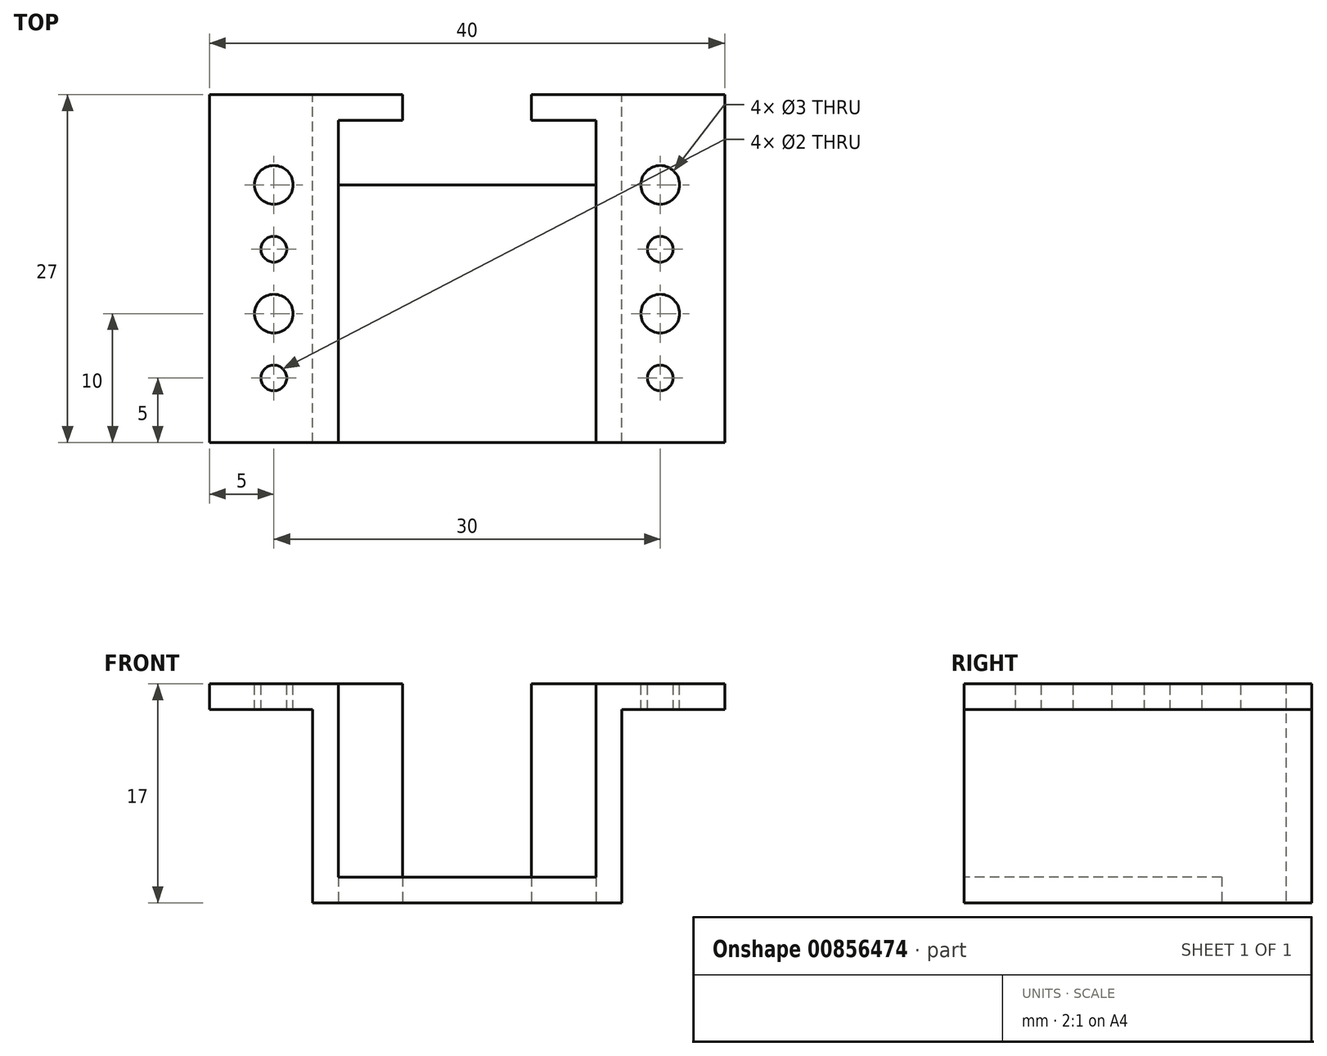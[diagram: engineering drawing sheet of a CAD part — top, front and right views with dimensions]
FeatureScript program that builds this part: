
annotation { "Feature Type Name" : "Feature", "Feature Type Description" : "" }
export const myFeature = defineFeature(function(context is Context, id is Id, definition is map)
    precondition{}
    {
        {
            var Q0;
            Q0=qCreatedBy(makeId("Front.planeOp"),FACE);
            var sketch = newSketch(context, id + "F0", { "sketchPlane" : qUnion([Q0])});
            skLineSegment(sketch, "E0.bottom", {"start": v(12, 0) * mm, "end": v(-12, 0) * mm});
            skLineSegment(sketch, "E0.top", {"start": v(12, -17) * mm, "end": v(-12, -17) * mm});
            skLineSegment(sketch, "E0.left", {"start": v(12, 0) * mm, "end": v(12, -17) * mm});
            skLineSegment(sketch, "E0.right", {"start": v(-12, 0) * mm, "end": v(-12, -17) * mm});
            skLineSegment(sketch, "E1.bottom", {"start": v(20, 0) * mm, "end": v(-20, 0) * mm});
            skLineSegment(sketch, "E1.top", {"start": v(20, -2) * mm, "end": v(-20, -2) * mm});
            skLineSegment(sketch, "E1.left", {"start": v(20, 0) * mm, "end": v(20, -2) * mm});
            skLineSegment(sketch, "E1.right", {"start": v(-20, 0) * mm, "end": v(-20, -2) * mm});
            skSolve(sketch);
        }
        {
            var Q0;
            Q0 = qSketchRegion(id + "F0", true);
            extrude(context, id + "F1", {"entities" : qUnion([Q0]), "depth" : 27 * mm, "offsetDistance" : 25 * mm});
        }
        {
            var Q0;
            Q0=makeQuery(id+"F1.opExtrude","SWEPT_FACE",FACE,{"disambiguationData":[OSD([sQuery(id+"F0.wireOp",EDGE,"E0.top")])]});
            var sketch = newSketch(context, id + "F2", { "sketchPlane" : qUnion([Q0])});
            skLineSegment(sketch, "E2.bottom", {"start": v(10, 2) * mm, "end": v(-10, 2) * mm});
            skLineSegment(sketch, "E2.top", {"start": v(10, 7) * mm, "end": v(-10, 7) * mm});
            skLineSegment(sketch, "E2.left", {"start": v(10, 2) * mm, "end": v(10, 7) * mm});
            skLineSegment(sketch, "E2.right", {"start": v(-10, 2) * mm, "end": v(-10, 7) * mm});
            skPoint(sketch, "E3.centerSnap0", {"position": v(0, 27) * mm});
            skLineSegment(sketch, "E4", {"start": v(0, 7) * mm, "end": v(0, 27) * mm, "construction": true});
            skSolve(sketch);
        }
        {
            var Q0;
            Q0 = qSketchRegion(id + "F2", true);
            extrude(context, id + "F3", {"entities" : qUnion([Q0]), "operationType" : NewBodyOperationType.REMOVE, "endBound" : BoundingType.THROUGH_ALL, "oppositeDirection" : true, "depth" : 25 * mm, "offsetDistance" : 25 * mm});
        }
        {
            var Q0;
            Q0=makeQuery(id+"F1.opExtrude","CAP_FACE",FACE,{"disambiguationData":[OSD([sQuery(id+"F0.wireOp",EDGE,"E0.top"),sQuery(id+"F0.wireOp",EDGE,"E0.left"),sQuery(id+"F0.wireOp",EDGE,"E0.right"),sQuery(id+"F0.wireOp",EDGE,"E1.bottom"),sQuery(id+"F0.wireOp",EDGE,"E1.top"),sQuery(id+"F0.wireOp",EDGE,"E1.left"),sQuery(id+"F0.wireOp",EDGE,"E1.right")])],"isStart":true});
            var sketch = newSketch(context, id + "F4", { "sketchPlane" : qUnion([Q0])});
            skLineSegment(sketch, "E5.bottom", {"start": v(-5, 0) * mm, "end": v(5, 0) * mm});
            skLineSegment(sketch, "E5.top", {"start": v(-5, -17) * mm, "end": v(5, -17) * mm});
            skLineSegment(sketch, "E5.left", {"start": v(-5, 0) * mm, "end": v(-5, -17) * mm});
            skLineSegment(sketch, "E5.right", {"start": v(5, 0) * mm, "end": v(5, -17) * mm});
            skSolve(sketch);
        }
        {
            var Q0;
            Q0 = qSketchRegion(id + "F4", true);
            extrude(context, id + "F5", {"entities" : qUnion([Q0]), "operationType" : NewBodyOperationType.REMOVE, "endBound" : BoundingType.UP_TO_NEXT, "oppositeDirection" : true, "depth" : 25 * mm, "offsetDistance" : 25 * mm});
        }
        {
            var Q0;
            Q0=makeQuery(id+"F1.opExtrude","CAP_FACE",FACE,{"disambiguationData":[OSD([sQuery(id+"F0.wireOp",EDGE,"E0.top"),sQuery(id+"F0.wireOp",EDGE,"E0.left"),sQuery(id+"F0.wireOp",EDGE,"E0.right"),sQuery(id+"F0.wireOp",EDGE,"E1.bottom"),sQuery(id+"F0.wireOp",EDGE,"E1.top"),sQuery(id+"F0.wireOp",EDGE,"E1.left"),sQuery(id+"F0.wireOp",EDGE,"E1.right")])],"isStart":false});
            var sketch = newSketch(context, id + "F6", { "sketchPlane" : qUnion([Q0])});
            skLineSegment(sketch, "E6.bottom", {"start": v(10, -15) * mm, "end": v(-10, -15) * mm});
            skLineSegment(sketch, "E6.top", {"start": v(10, -2) * mm, "end": v(-10, -2) * mm});
            skLineSegment(sketch, "E6.left", {"start": v(10, -15) * mm, "end": v(10, -2) * mm});
            skLineSegment(sketch, "E6.right", {"start": v(-10, -15) * mm, "end": v(-10, -2) * mm});
            skSolve(sketch);
        }
        {
            var Q0;
            Q0 = qSketchRegion(id + "F6", true);
            var Q1;
            Q1=makeQuery(id+"F5.boolean.opBoolean","SPLIT",FACE,{"disambiguationData":[TD([makeQuery(id+"F3.boolean.opBoolean","COPY",FACE,{"derivedFrom":makeQuery(id+"F3.opExtrude","SWEPT_FACE",FACE,{"disambiguationData":[OSD([sQuery(id+"F2.wireOp",EDGE,"E2.right")])]})})])],"derivedFrom":makeQuery(id+"F3.boolean.opBoolean","COPY",FACE,{"derivedFrom":makeQuery(id+"F3.opExtrude","SWEPT_FACE",FACE,{"disambiguationData":[OSD([sQuery(id+"F2.wireOp",EDGE,"E2.bottom")])]})})});
            extrude(context, id + "F7", {"entities" : qUnion([Q0]), "operationType" : NewBodyOperationType.REMOVE, "endBound" : BoundingType.UP_TO_SURFACE, "oppositeDirection" : true, "depth" : 25 * mm, "endBoundEntityFace" : qUnion([Q1]), "offsetDistance" : 25 * mm});
        }
        {
            var Q0;
            Q0=makeQuery(id+"F1.opExtrude","SWEPT_FACE",FACE,{"disambiguationData":[OSD([sQuery(id+"F0.wireOp",EDGE,"E1.bottom")])]});
            var sketch = newSketch(context, id + "F8", { "sketchPlane" : qUnion([Q0])});
            skLineSegment(sketch, "E7.bottom", {"start": v(-10, -2) * mm, "end": v(10, -2) * mm});
            skLineSegment(sketch, "E7.top", {"start": v(-10, -27) * mm, "end": v(10, -27) * mm});
            skLineSegment(sketch, "E7.left", {"start": v(-10, -2) * mm, "end": v(-10, -27) * mm});
            skLineSegment(sketch, "E7.right", {"start": v(10, -2) * mm, "end": v(10, -27) * mm});
            skSolve(sketch);
        }
        {
            var Q0;
            {var subQ0=sQuery(id+"F8.wireOp",EDGE,"E7.top");Q0=makeQuery(id+"F8.imprint","IMPRINT",FACE,{"disambiguationData":[TD([[makeQuery(id+"F8.imprint","IMPRINT",EDGE,{"derivedFrom":subQ0}),-1.0]])]});}
            var Q1;
            {var subQ1=makeQuery(id+"F1.opExtrude","SWEPT_FACE",FACE,{"disambiguationData":[OSD([sQuery(id+"F0.wireOp",EDGE,"E1.bottom")])]});var subQ2=makeQuery(id+"F3.boolean.opBoolean","INTERSECT",EDGE,{"derivedFrom":[subQ1,makeQuery(id+"F3.opExtrude","SWEPT_FACE",FACE,{"disambiguationData":[OSD([sQuery(id+"F2.wireOp",EDGE,"E2.top")])]})]});Q1=makeQuery(id+"F8.imprint","IMPRINT",FACE,{"disambiguationData":[TD([[makeQuery(id+"F8.imprint","IMPRINT",EDGE,{"derivedFrom":subQ2}),1.0]])]});}
            extrude(context, id + "F9", {"entities" : qUnion([Q0, Q1]), "operationType" : NewBodyOperationType.REMOVE, "endBound" : BoundingType.UP_TO_NEXT, "oppositeDirection" : true, "depth" : 25 * mm, "offsetDistance" : 25 * mm});
        }
        {
            var Q0;
            {var subQ0=sQuery(id+"F0.wireOp",EDGE,"E1.left");var subQ3=sQuery(id+"F0.wireOp",EDGE,"E1.bottom");var subQ8=makeQuery(id+"F1.opExtrude","SWEPT_FACE",FACE,{"disambiguationData":[OSD([subQ3])]});Q0=makeQuery(id+"F9.boolean.opBoolean","SPLIT",FACE,{"disambiguationData":[TD([makeQuery(id+"F1.opExtrude","SWEPT_FACE",FACE,{"disambiguationData":[OSD([subQ0])]})])],"derivedFrom":subQ8});}
            var sketch = newSketch(context, id + "F10", { "sketchPlane" : qUnion([Q0])});
            skCircle(sketch, "E8", {"center": v(15, -22) * mm, "radius": 1 * mm});
            skPoint(sketch, "E8.centerSnap0", {"position": v(15, -27) * mm});
            skCircle(sketch, "E9", {"center": v(15, -17) * mm, "radius": 1.5 * mm});
            skCircle(sketch, "E10", {"center": v(15, -12) * mm, "radius": 1 * mm});
            skCircle(sketch, "E11", {"center": v(15, -7) * mm, "radius": 1.5 * mm});
            skSolve(sketch);
        }
        {
            var Q0;
            Q0 = qSketchRegion(id + "F10", true);
            extrude(context, id + "F11", {"entities" : qUnion([Q0]), "operationType" : NewBodyOperationType.REMOVE, "endBound" : BoundingType.THROUGH_ALL, "oppositeDirection" : true, "depth" : 25 * mm, "offsetDistance" : 25 * mm});
        }
        {
            var Q0;
            {var subQ0=sQuery(id+"F0.wireOp",EDGE,"E1.right");var subQ2=sQuery(id+"F0.wireOp",EDGE,"E1.bottom");var subQ3=makeQuery(id+"F1.opExtrude","SWEPT_FACE",FACE,{"disambiguationData":[OSD([subQ2])]});Q0=makeQuery(id+"F9.boolean.opBoolean","SPLIT",FACE,{"disambiguationData":[TD([makeQuery(id+"F1.opExtrude","SWEPT_FACE",FACE,{"disambiguationData":[OSD([subQ0])]})])],"derivedFrom":subQ3});}
            var sketch = newSketch(context, id + "F12", { "sketchPlane" : qUnion([Q0])});
            skCircle(sketch, "E12", {"center": v(-15, -22) * mm, "radius": 1 * mm});
            skPoint(sketch, "E12.centerSnap0", {"position": v(-15, -27) * mm});
            skCircle(sketch, "E13", {"center": v(-15, -17) * mm, "radius": 1.5 * mm});
            skCircle(sketch, "E14", {"center": v(-15, -12) * mm, "radius": 1 * mm});
            skCircle(sketch, "E15", {"center": v(-15, -7) * mm, "radius": 1.5 * mm});
            skSolve(sketch);
        }
        {
            var Q0;
            Q0 = qSketchRegion(id + "F12", true);
            extrude(context, id + "F13", {"entities" : qUnion([Q0]), "operationType" : NewBodyOperationType.REMOVE, "endBound" : BoundingType.THROUGH_ALL, "oppositeDirection" : true, "depth" : 25 * mm, "offsetDistance" : 25 * mm});
        }
    });
